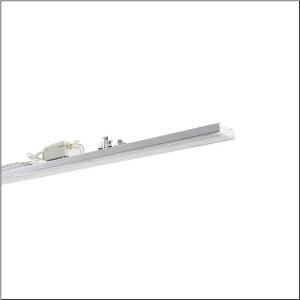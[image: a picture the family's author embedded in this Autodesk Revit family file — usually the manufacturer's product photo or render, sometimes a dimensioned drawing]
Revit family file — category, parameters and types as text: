
# Revit family: licross_21_recessed_mo_52tl1edn455g
name_source: partatom
category: Lighting Fixtures
units: mm (PartAtom-declared; Revit-internal decimal feet)

## family parameters
Cut with Voids When Loaded = No
Host = Face
Light Source = No
Part Type = Normal
Room Calculation Point = No
Round Connector Dimension = Use Diameter
Shared = No

## types (1)
- --- (1 x LED, 5800 lm, 32.4 W, 4000K)
    Apparent Load = 32 VA
    CIE Flux Codes = 85 95 99 100 100
    Color Rendering = 80
    Color Temperature = 4000K
    Default Elevation = 1800 mm
    Description = Licross 21 Recessed MO, luminaire insert, of sheet steel, galvanised, coil coated, white, length: 1.500mm, width: 66mm, height: 67mm, LED rated luminous flux: 5.800lm, light colour: 840, SDCM (Standard Deviation of Colour Matching)MacAdam ≤ 3 SDCM (initial), control gear: DALI 2, with plug, 5-pole, with phase selection, mains connection: 220..240V, AC, 50/60Hz, rated input power: 32W, internal wiring halogen-free, primary light control with lens, of plastic, primary optical cover: cover, of PMMA, light emission: direct distribution, primary light characteristic: symmetric, protection rating (complete): IP40, insulation class (complete): insulation class I (protective earthing), certification: CE, ENEC, VDE, UKCA, protection symbol: D if used in an environment without relevant dust loads with corresponding accessories, impact resistance: IK06, permissible ambient temperature for indoor applications: -25..+45°C, corresponds to IFS (International Featured Standards) requirements for safety and quality in the food industry, reducing of maximum allowable ambient temperature of 5°C with ceiling mounting, LABS conformity tested according to VDMA 24364:2018-05, The light source and the operating device comply with the requirements of the Ecodesign Regulation (EU) 2019/2020 and are replaceable in accordance with this regulation, packaging unit: 1 piece
    Height = 58 mm
    Lamp = 1 x LED
    Lamp Light Flux = 5800 lm
    Lamp Power = 32.4 W
    Lamp count = 1
    Length = 1500 mm
    Luminous efficacy = 179 lm/W
    Manufacturer = Siteco
    ModVariant = No
    Model = 52TL1EDN455G
    Mounting Place = Ceiling
    Mounting Type = Pendant
    Number of Poles = 1
    OnlyDefault = Yes
    Power Factor = 1
    Product Name = Licross 21 Recessed MO
    Product group = luminaire insert | ceiling pendant
    ProductGroupID = 901
    Protection Class = Protection class I
    Protection Degree = IP 40
    RLX_Detail_Level = 1
    RLX_Emergency_Light_Flux = 0 lm
    RLX_Emergency_Type = 0
    RLX_Emergency_Type_DB = No
    RlxData = <blob elided: 24601 chars, md5=caa9e70e>
    Socket = socket
    Standby Power = 0 W
    System Light Flux = 5800 lm
    System Power = 32 W
    Type Comments = factory setting: luminous flux: 100 % | dim-lin: 254 | 219 mA
    Type Image = l_1296930.jpg
    URL = http://relux.com
    VarID = @adj_127027
    Voltage = 0 V
    Weight = 0.00 kg
    Width = 66 mm

## geometry (parser evidence)
native form markers: Blend x4, Sweep x14
no freeform markers — native parametric forms only
